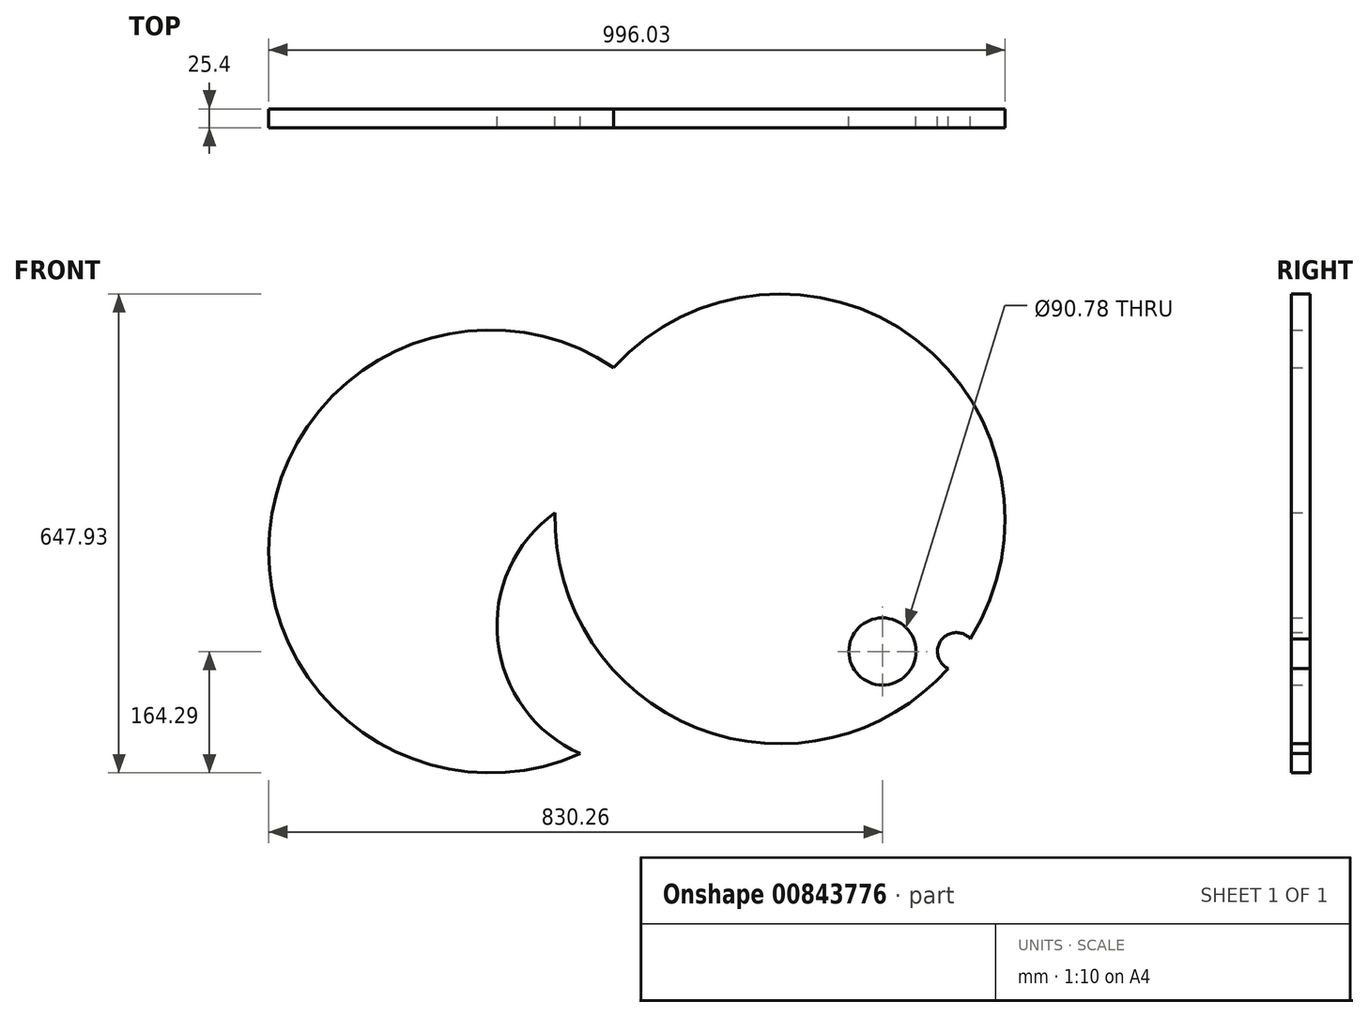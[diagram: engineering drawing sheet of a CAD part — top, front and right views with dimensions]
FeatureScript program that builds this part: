
annotation { "Feature Type Name" : "Feature", "Feature Type Description" : "" }
export const myFeature = defineFeature(function(context is Context, id is Id, definition is map)
    precondition{}
    {
        {
            var Q0;
            Q0=qCreatedBy(makeId("Front.planeOp"),FACE);
            var sketch = newSketch(context, id + "F0", { "sketchPlane" : qUnion([Q0])});
            skCircle(sketch, "E0", {"center": v(0, 0) * mm, "radius": 45.39 * mm});
            skCircle(sketch, "E1", {"center": v(100.04, 0) * mm, "radius": 25.49 * mm});
            skCircle(sketch, "E2", {"center": v(-138.58, 179.29) * mm, "radius": 304.35 * mm});
            skSolve(sketch);
        }
        {
            var Q0;
            Q0=makeQuery(id+"F0.imprint","IMPRINT",FACE,{"disambiguationData":[TD([[makeQuery(id+"F0.imprint","IMPRINT",EDGE,{"derivedFrom":sQuery(id+"F0.wireOp",EDGE,"E0")}),-1.0]])]});
            var sketch = newSketch(context, id + "F1", { "sketchPlane" : qUnion([Q0])});
            skArc(sketch, "E3", {"start": v(-237.66, 197.86) * mm, "mid": v(-504.21, -44.24) * mm, "end": v(-146.86, 0) * mm});
            skArc(sketch, "E4", {"start": v(-237.66, 197.86) * mm, "mid": v(-829.62, 154.86) * mm, "end": v(-248.3, 35.14) * mm});
            skSolve(sketch);
        }
        {
            var Q0;
            Q0 = qSketchRegion(id + "F1", true);
            extrude(context, id + "F2", {"entities" : qUnion([Q0]), "depth" : 25.4 * mm, "offsetDistance" : 25.4 * mm});
        }
        {
            var Q0;
            Q0=makeQuery(id+"F0.imprint","IMPRINT",FACE,{"disambiguationData":[TD([[makeQuery(id+"F0.imprint","IMPRINT",EDGE,{"derivedFrom":sQuery(id+"F0.wireOp",EDGE,"E0")}),-1.0]])]});
            extrude(context, id + "F3", {"entities" : qUnion([Q0]), "operationType" : NewBodyOperationType.ADD, "depth" : 25.4 * mm, "offsetDistance" : 25.4 * mm});
        }
    });
